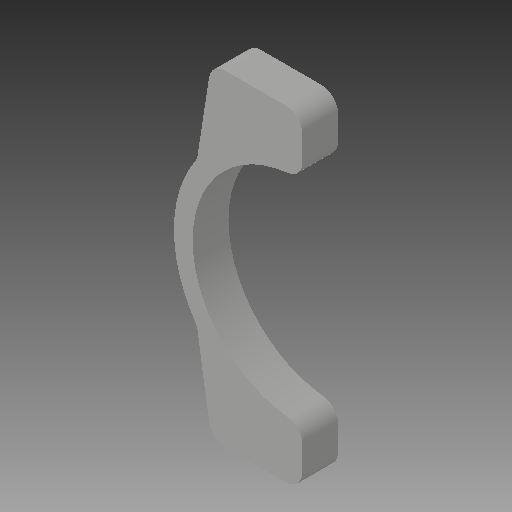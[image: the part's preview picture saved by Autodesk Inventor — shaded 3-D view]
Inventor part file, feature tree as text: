
AUTODESK INVENTOR PART (.ipt)
format: ipt  version: 2019 (Build 230136000, 136)  size: 144,896 bytes
history: native  units: in
note: dims shown in document units (in); Inventor stores cm internally (conversion verified against a paired STEP export)
features: reference x11, thicken_offset x2, other x2, extrude x1, fillet x1, sketch x1
ambient origin geometry x8: Origin, YZ Plane, XZ Plane, XY Plane, X Axis, Y Axis, Z Axis, Center Point
bodies: Solid1 (feature_tree)
feature tree (18):
  extrude  "Extrusion1"  Depth=0.173in TaperAngle=0.0deg
  thicken_offset  "Thicken1"
  thicken_offset  "Thicken2"
  fillet  "Fillet1"  Radius=0.0787in
  sketch  "Sketch1"  dims[d0=0.4331in d1=0.173in d2=0.0in d3=0.0787in d4=0.0394in d5=0.0394in d6=0.0394in d7=0.0394in]
  reference  "Reference1"
  reference  "Reference2"
  reference  "Reference3"
  reference  "Reference4"
  reference  "Reference5"
  reference  "Reference6"
  reference  "Reference7"
  reference  "Reference8"
  reference  "Reference9"
  reference  "Reference10"
  reference  "Reference11"
  parser-record x1  (decoder bookkeeping rows leaked as tree rows — omitted from the tree; the rows remain in map.json)
  other  "zplate_assembly.iam"
note: 1 file-system path scrubbed to <path> (originals preserved in map.json)
